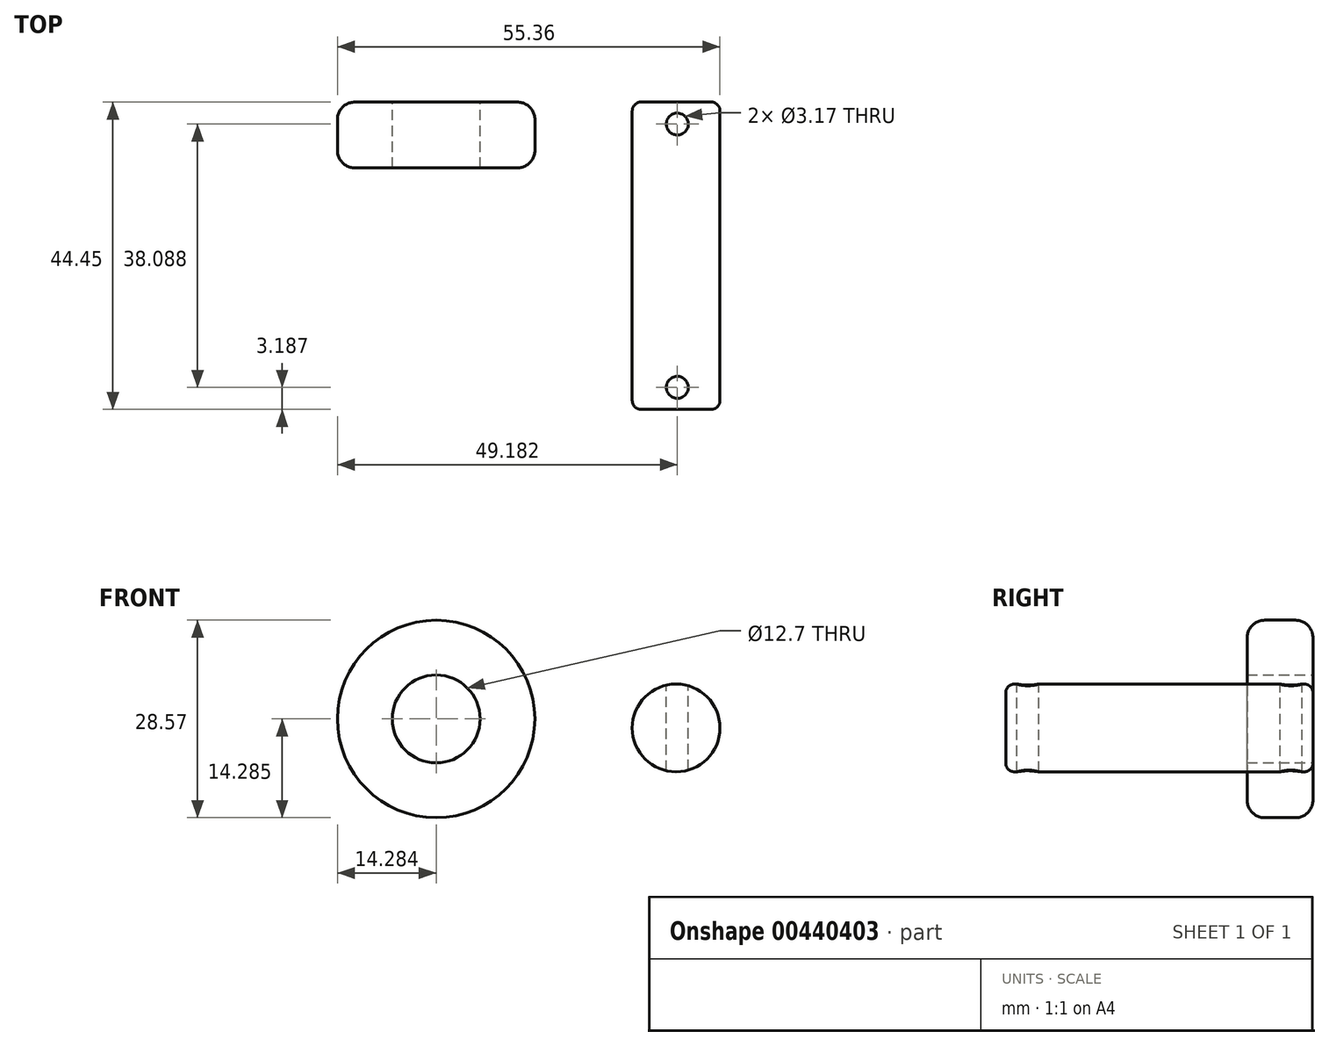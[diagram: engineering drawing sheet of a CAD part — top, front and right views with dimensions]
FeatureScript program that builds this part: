
annotation { "Feature Type Name" : "Feature", "Feature Type Description" : "" }
export const myFeature = defineFeature(function(context is Context, id is Id, definition is map)
    precondition{}
    {
        {
            var Q0;
            Q0=qCreatedBy(makeId("Front.planeOp"),FACE);
            var sketch = newSketch(context, id + "F0", { "sketchPlane" : qUnion([Q0])});
            skCircle(sketch, "E0", {"center": v(25.75, 26.9) * mm, "radius": 6.35 * mm});
            skCircle(sketch, "E1", {"center": v(25.75, 26.9) * mm, "radius": 14.29 * mm});
            skSolve(sketch);
        }
        {
            var Q0;
            Q0=makeQuery(id+"F0.imprint","IMPRINT",FACE,{"disambiguationData":[TD([[makeQuery(id+"F0.imprint","IMPRINT",EDGE,{"derivedFrom":sQuery(id+"F0.wireOp",EDGE,"E0")}),-1.0]])]});
            extrude(context, id + "F1", {"entities" : qUnion([Q0]), "flatOperationType" : FlatOperationType.REMOVE, "offsetDistance" : 25.4 * mm, "depth" : 9.52 * mm, "domain" : OperationDomain.MODEL});
        }
        {
            var Q0;
            Q0=makeQuery(id+"F1.opExtrude","CAP_EDGE",EDGE,{"disambiguationData":[OSD([sQuery(id+"F0.wireOp",EDGE,"E1")])],"isStart":false});
            fillet(context, id + "F2", {"entities" : qUnion([Q0]), "radius" : 2.54 * mm, "tangentPropagation" : true, "allowEdgeOverflow" : false});
        }
        {
            var Q0;
            Q0=makeQuery(id+"F1.opExtrude","CAP_EDGE",EDGE,{"disambiguationData":[OSD([sQuery(id+"F0.wireOp",EDGE,"E1")])],"isStart":true});
            fillet(context, id + "F3", {"entities" : qUnion([Q0]), "radius" : 2.54 * mm, "tangentPropagation" : true, "allowEdgeOverflow" : false});
        }
        {
            var Q0;
            Q0=qCreatedBy(makeId("Front.planeOp"),FACE);
            var sketch = newSketch(context, id + "F4", { "sketchPlane" : qUnion([Q0])});
            skCircle(sketch, "E2", {"center": v(60.48, 25.6) * mm, "radius": 6.35 * mm});
            skSolve(sketch);
        }
        {
            var Q0;
            Q0=makeQuery(id+"F4.imprint","IMPRINT",FACE,{"disambiguationData":[TD([[makeQuery(id+"F4.imprint","IMPRINT",EDGE,{"derivedFrom":sQuery(id+"F4.wireOp",EDGE,"E2")}),1.0]])]});
            extrude(context, id + "F5", {"entities" : qUnion([Q0]), "depth" : 44.45 * mm});
        }
        {
            var Q0;
            Q0=makeQuery(id+"F5.opExtrude","CAP_EDGE",EDGE,{"disambiguationData":[OSD([sQuery(id+"F4.wireOp",EDGE,"E2")])],"isStart":false});
            var Q1;
            Q1=makeQuery(id+"F5.opExtrude","CAP_EDGE",EDGE,{"disambiguationData":[OSD([sQuery(id+"F4.wireOp",EDGE,"E2")])],"isStart":true});
            fillet(context, id + "F6", {"entities" : qUnion([Q0, Q1]), "radius" : 1.27 * mm, "tangentPropagation" : true, "allowEdgeOverflow" : false});
        }
        {
            var Q0;
            Q0=qCreatedBy(makeId("Top.planeOp"),FACE);
            var sketch = newSketch(context, id + "F7", { "sketchPlane" : qUnion([Q0])});
            skPoint(sketch, "E3", {"position": v(60.65, -41.26) * mm});
            skPoint(sketch, "E4", {"position": v(60.65, -3.18) * mm});
            skLineSegment(sketch, "E5", {"start": v(60.65, 0) * mm, "end": v(60.65, -3.18) * mm});
            skLineSegment(sketch, "E6", {"start": v(60.65, -44.44) * mm, "end": v(60.65, -41.26) * mm});
            skSolve(sketch);
        }
        {
            var Q0;
            Q0=sQuery(id+"F7.wireOp",VERTEX,"E3");
            var Q1;
            Q1=sQuery(id+"F7.wireOp",VERTEX,"E4");
            var Q2;
            Q2=makeQuery(id+"F5.opExtrude","SWEPT_BODY",BODY,{"disambiguationData":[OSD([sQuery(id+"F4.wireOp",EDGE,"E2")])]});
            hole(context, id + "F8", {"style" : HoleStyle.SIMPLE, "endStyle" : HoleEndStyle.THROUGH, "oppositeDirection" : true, "holeDiameter" : 3.17 * mm, "isTappedThrough" : true, "tappedDepth" : 12.7 * mm, "tapClearance" : 3, "startFromSketch" : true, "locations" : qUnion([Q0, Q1]), "scope" : qUnion([Q2])});
        }
    });
